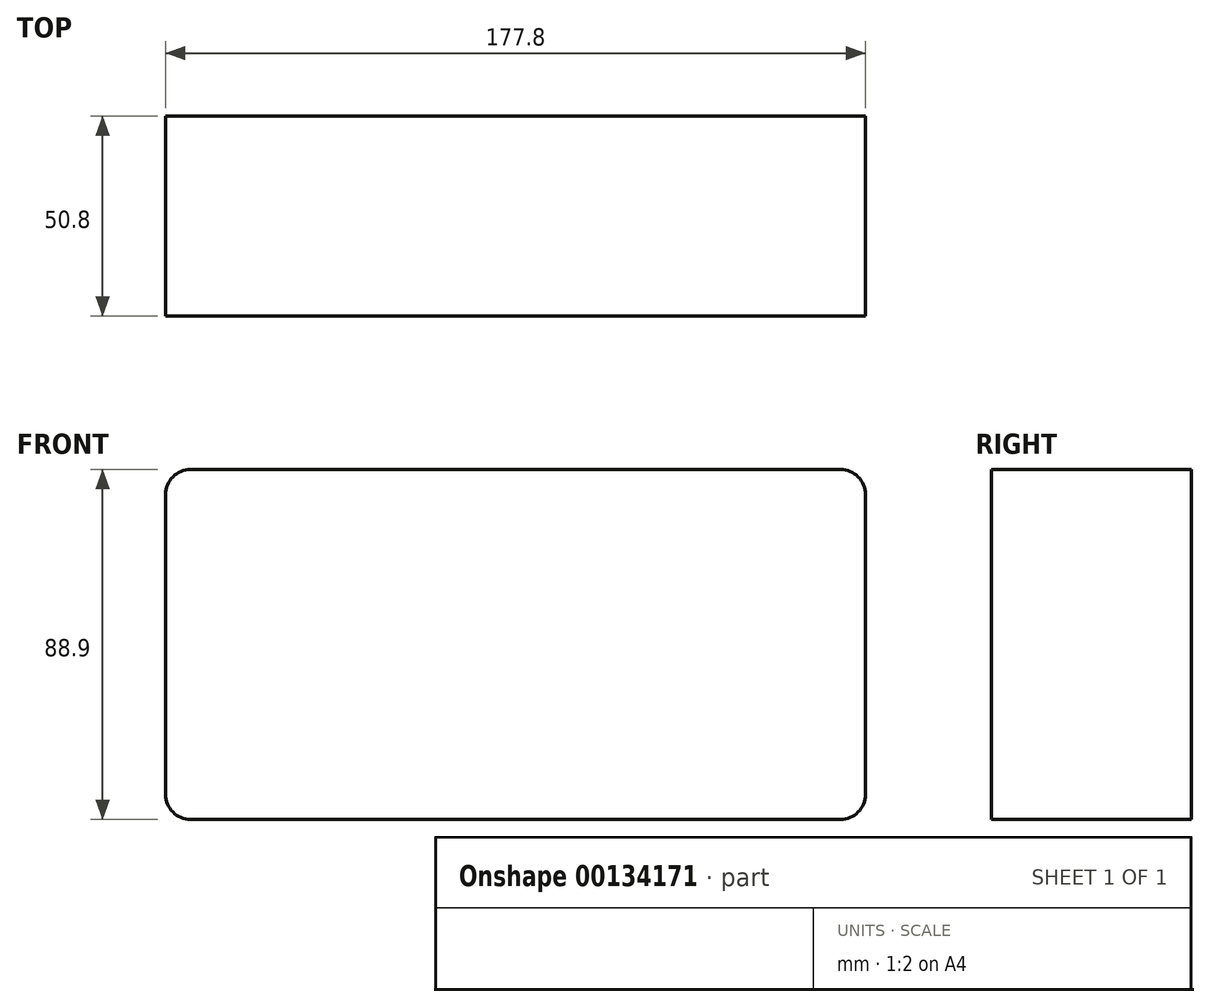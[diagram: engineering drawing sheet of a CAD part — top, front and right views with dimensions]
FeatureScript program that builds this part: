
annotation { "Feature Type Name" : "Feature", "Feature Type Description" : "" }
export const myFeature = defineFeature(function(context is Context, id is Id, definition is map)
    precondition{}
    {
        {
            var Q0;
            Q0=qCreatedBy(makeId("Front.planeOp"),FACE);
            var sketch = newSketch(context, id + "F0", { "sketchPlane" : qUnion([Q0])});
            skLineSegment(sketch, "E0.bottom", {"start": v(6.35, 0) * mm, "end": v(171.45, 0) * mm});
            skLineSegment(sketch, "E0.top", {"start": v(6.35, 88.9) * mm, "end": v(171.45, 88.9) * mm});
            skLineSegment(sketch, "E0.left", {"start": v(0, 6.35) * mm, "end": v(0, 82.55) * mm});
            skLineSegment(sketch, "E0.right", {"start": v(177.8, 6.35) * mm, "end": v(177.8, 82.55) * mm});
            skPoint(sketch, "E1.visualSharp", {"position": v(0, 88.9) * mm});
            skArc(sketch, "E1.filletArc", {"start": v(6.35, 88.9) * mm, "mid": v(1.86, 87.04) * mm, "end": v(0, 82.55) * mm});
            skPoint(sketch, "E2.visualSharp", {"position": v(0, 0) * mm});
            skArc(sketch, "E2.filletArc", {"start": v(0, 6.35) * mm, "mid": v(1.86, 1.86) * mm, "end": v(6.35, 0) * mm});
            skPoint(sketch, "E3.visualSharp", {"position": v(177.8, 88.9) * mm});
            skArc(sketch, "E3.filletArc", {"start": v(177.8, 82.55) * mm, "mid": v(175.94, 87.04) * mm, "end": v(171.45, 88.9) * mm});
            skPoint(sketch, "E4.visualSharp", {"position": v(177.8, 0) * mm});
            skArc(sketch, "E4.filletArc", {"start": v(171.45, 0) * mm, "mid": v(175.94, 1.86) * mm, "end": v(177.8, 6.35) * mm});
            skSolve(sketch);
        }
        {
            var Q0;
            Q0 = qSketchRegion(id + "F0", true);
            extrude(context, id + "F1", {"entities" : qUnion([Q0]), "depth" : 50.8 * mm});
        }
    });
